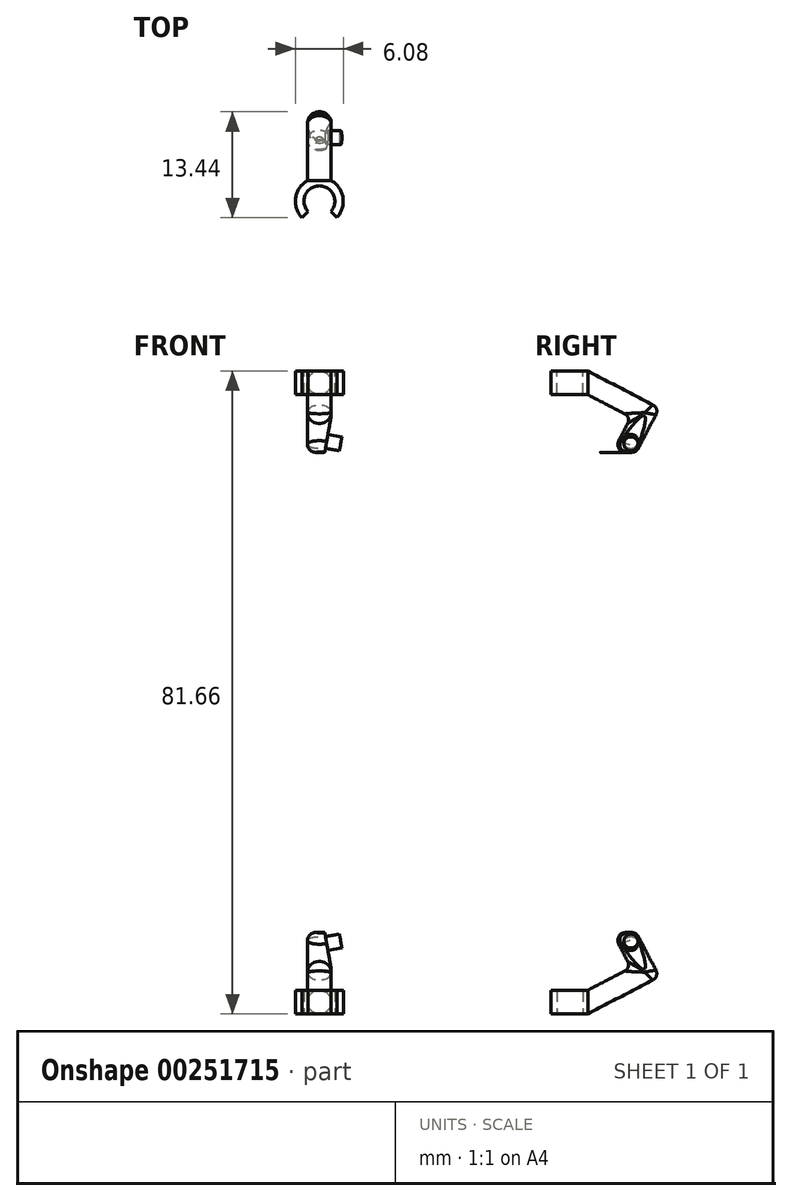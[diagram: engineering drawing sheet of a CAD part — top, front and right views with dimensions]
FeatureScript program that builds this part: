
annotation { "Feature Type Name" : "Feature", "Feature Type Description" : "" }
export const myFeature = defineFeature(function(context is Context, id is Id, definition is map)
    precondition{}
    {
        {
            var Q0;
            Q0=qCreatedBy(makeId("Top.planeOp"),FACE);
            var sketch = newSketch(context, id + "F0", { "sketchPlane" : qUnion([Q0])});
            skCircle(sketch, "E0", {"center": v(0, 0) * mm, "radius": 5 * mm});
            skSolve(sketch);
        }
        {
            var Q0;
            Q0=qCreatedBy(makeId("Right.planeOp"),FACE);
            var sketch = newSketch(context, id + "F1", { "sketchPlane" : qUnion([Q0])});
            skLineSegment(sketch, "E1", {"start": v(0, 0) * mm, "end": v(8.74, -16.81) * mm});
            skLineSegment(sketch, "E2", {"start": v(8.74, -16.81) * mm, "end": v(-15.53, -29.43) * mm});
            skSolve(sketch);
        }
        {
            var Q0;
            Q0=makeQuery(id+"F0.imprint","IMPRINT",FACE,{"disambiguationData":[TD([[makeQuery(id+"F0.imprint","IMPRINT",EDGE,{"derivedFrom":sQuery(id+"F0.wireOp",EDGE,"E0")}),1.0]])]});
            var Q1;
            Q1=sQuery(id+"F1.wireOp",EDGE,"E1");
            var Q2;
            Q2=sQuery(id+"F1.wireOp",EDGE,"E2");
            sweep(context, id + "F2", {"profiles" : qUnion([Q0]), "path" : qUnion([Q1, Q2])});
        }
        {
            var Q0;
            Q0=makeQuery(id+"F2.opSweep","MID_CAP_EDGE",EDGE,{"disambiguationData":[OSD([sQuery(id+"F0.wireOp",EDGE,"E0"),sQuery(id+"F1.wireOp",VERTEX,"E2.start")])],"capPos":1.0});
            fillet(context, id + "F3", {"entities" : qUnion([Q0]), "radius" : 3 * mm, "tangentPropagation" : true, "allowEdgeOverflow" : false});
        }
        {
            var Q0;
            Q0=makeQuery(id+"F2.opSweep","CAP_EDGE",EDGE,{"disambiguationData":[OSD([sQuery(id+"F0.wireOp",EDGE,"E0"),sQuery(id+"F1.wireOp",VERTEX,"E1.start")])],"isStart":true});
            fillet(context, id + "F4", {"entities" : qUnion([Q0]), "radius" : 3.38 * mm, "tangentPropagation" : true, "allowEdgeOverflow" : false});
        }
        {
            var Q0;
            Q0=qCreatedBy(makeId("Front.planeOp"),FACE);
            var sketch = newSketch(context, id + "F5", { "sketchPlane" : qUnion([Q0])});
            skLineSegment(sketch, "E3", {"start": v(2.03, 1.57) * mm, "end": v(31.42, 1.57) * mm});
            skLineSegment(sketch, "E4", {"start": v(2.03, 1.57) * mm, "end": v(5.73, -19.69) * mm});
            skLineSegment(sketch, "E5", {"start": v(5.73, -19.69) * mm, "end": v(31.42, 1.57) * mm});
            skSolve(sketch);
        }
        {
            var Q0;
            Q0 = qSketchRegion(id + "F5", true);
            extrude(context, id + "F6", {"entities" : qUnion([Q0]), "operationType" : NewBodyOperationType.REMOVE, "oppositeDirection" : true, "depth" : 33 * mm, "hasSecondDirection" : true, "secondDirectionOppositeDirection" : false, "secondDirectionDepth" : 37.2 * mm});
        }
        {
            var Q0;
            Q0=makeQuery(id+"F2.opSweep","CAP_FACE",FACE,{"disambiguationData":[OSD([sQuery(id+"F0.wireOp",EDGE,"E0"),sQuery(id+"F1.wireOp",VERTEX,"E2.end")])],"isStart":false});
            var sketch = newSketch(context, id + "F7", { "sketchPlane" : qUnion([Q0])});
            skCircle(sketch, "E6.0.0", {"center": v(0, -29.43) * mm, "radius": 5 * mm, "construction": true});
            skLineSegment(sketch, "E7", {"start": v(-11.73, -29.43) * mm, "end": v(10.87, -29.43) * mm, "construction": true});
            skSolve(sketch);
        }
        {
            var Q0;
            Q0=sQuery(id+"F7.wireOp",EDGE,"E7");
            cPlane(context, id + "F8", {"entities" : qUnion([Q0]), "cplaneType" : CPlaneType.LINE_ANGLE, "offset" : 25 * mm, "angle" : 90 * degree, "width" : 150 * mm, "height" : 150 * mm});
        }
        {
            var Q0;
            Q0=qCreatedBy(id+"F8.planeOp",FACE);
            var sketch = newSketch(context, id + "F9", { "sketchPlane" : qUnion([Q0])});
            skLineSegment(sketch, "E8.0", {"start": v(-11.73, -15.53) * mm, "end": v(10.87, -15.53) * mm});
            skArc(sketch, "E9", {"start": v(7.4, -31.14) * mm, "mid": v(10.02, -22.8) * mm, "end": v(5.17, -15.53) * mm});
            skArc(sketch, "E10", {"start": v(4.89, -28.57) * mm, "mid": v(0, -17.69) * mm, "end": v(-4.89, -28.57) * mm});
            skLineSegment(sketch, "E11", {"start": v(-7.4, -31.14) * mm, "end": v(-4.89, -28.57) * mm});
            skLineSegment(sketch, "E12", {"start": v(4.89, -28.57) * mm, "end": v(7.4, -31.14) * mm});
            skPoint(sketch, "E13", {"position": v(0, -30.77) * mm});
            skArc(sketch, "E14.trimOffspring", {"start": v(-5.17, -15.53) * mm, "mid": v(-10.02, -22.8) * mm, "end": v(-7.4, -31.14) * mm});
            skSolve(sketch);
        }
        {
            var Q0;
            {var subQ0=sQuery(id+"F9.wireOp",EDGE,"E9");Q0=makeQuery(id+"F9.imprint","IMPRINT",FACE,{"disambiguationData":[TD([[makeQuery(id+"F9.imprint","IMPRINT",EDGE,{"derivedFrom":subQ0}),1.0]])]});}
            extrude(context, id + "F10", {"entities" : qUnion([Q0]), "operationType" : NewBodyOperationType.ADD, "endBound" : BoundingType.SYMMETRIC, "depth" : 10 * mm});
        }
        {
            var Q0;
            Q0=qCreatedBy(makeId("Right.planeOp"),FACE);
            var sketch = newSketch(context, id + "F11", { "sketchPlane" : qUnion([Q0])});
            skLineSegment(sketch, "E15", {"start": v(-39.9, 13.4) * mm, "end": v(66.3, 13.4) * mm});
            skSolve(sketch);
        }
        {
            var Q0;
            Q0=sQuery(id+"F11.wireOp",EDGE,"E15");
            cPlane(context, id + "F12", {"entities" : qUnion([Q0]), "cplaneType" : CPlaneType.LINE_ANGLE, "offset" : 25 * mm, "angle" : 0 * degree, "width" : 150 * mm, "height" : 150 * mm});
        }
        {
            var Q0;
            Q0=makeQuery(id+"F2.opSweep","SWEPT_BODY",BODY,{"disambiguationData":[OSD([sQuery(id+"F0.wireOp",EDGE,"E0"),sQuery(id+"F1.wireOp",EDGE,"E2")])]});
            var Q1;
            {var subQ0=sQuery(id+"F9.wireOp",EDGE,"E8.0");Q1=makeQuery(id+"F10.boolean.opBoolean","TWEAK_VERTEX",VERTEX,{"derivedFrom":[makeQuery(id+"F2.opSweep","SWEPT_FACE",FACE,{"disambiguationData":[OSD([sQuery(id+"F0.wireOp",EDGE,"E0"),sQuery(id+"F1.wireOp",EDGE,"E2")])]}),makeQuery(id+"F10.opExtrude","SWEPT_FACE",FACE,{"disambiguationData":[OSD([subQ0])]}),makeQuery(id+"F10.opExtrude","CAP_FACE",FACE,{"disambiguationData":[OSD([subQ0,sQuery(id+"F9.wireOp",EDGE,"E9"),sQuery(id+"F9.wireOp",EDGE,"E10"),sQuery(id+"F9.wireOp",EDGE,"E11"),sQuery(id+"F9.wireOp",EDGE,"E12"),sQuery(id+"F9.wireOp",EDGE,"E14.trimOffspring")])],"isStart":false})]});}
            transform(context, id + "F13", {"entities" : qUnion([Q0]), "transformType" : TransformType.SCALE_UNIFORMLY, "scale" : 0.3, "scalePoint" : qUnion([Q1]), "makeCopy" : false});
        }
        {
            var Q0;
            Q0=makeQuery(id+"F6.boolean.opBoolean","COPY",FACE,{"derivedFrom":makeQuery(id+"F6.opExtrude","SWEPT_FACE",FACE,{"disambiguationData":[OSD([sQuery(id+"F5.wireOp",EDGE,"E4")])]})});
            var sketch = newSketch(context, id + "F14", { "sketchPlane" : qUnion([Q0])});
            skFitSpline(sketch, "E16.0.0", {"points": [v(-11.88, -17.49) * mm, v(-11.77, -17.67) * mm, v(-11.55, -18.02) * mm, v(-11.21, -18.54) * mm, v(-10.87, -19.06) * mm, v(-10.51, -19.57) * mm, v(-10.2, -20) * mm, v(-9.95, -20.32) * mm, v(-9.76, -20.56) * mm, v(-9.56, -20.8) * mm, v(-9.35, -21.04) * mm, v(-9.13, -21.26) * mm, v(-8.94, -21.43) * mm, v(-8.78, -21.56) * mm, v(-8.64, -21.64) * mm, v(-8.51, -21.68) * mm, v(-8.4, -21.68) * mm, v(-8.33, -21.65) * mm, v(-8.28, -21.6) * mm, v(-8.23, -21.5) * mm, v(-8.21, -21.36) * mm, v(-8.2, -21.2) * mm, v(-8.21, -21.05) * mm, v(-8.23, -20.9) * mm, v(-8.26, -20.7) * mm, v(-8.32, -20.44) * mm, v(-8.4, -20.13) * mm, v(-8.5, -19.74) * mm, v(-8.66, -19.24) * mm, v(-8.87, -18.65) * mm, v(-9.09, -18.07) * mm, v(-9.24, -17.68) * mm, v(-9.32, -17.49) * mm]});
            skFitSpline(sketch, "E16.0.1", {"points": [v(-9.28, -17.58) * mm, v(-9.3, -17.51) * mm, v(-9.38, -17.39) * mm, v(-9.58, -17.18) * mm, v(-9.84, -17.05) * mm, v(-10.12, -17) * mm, v(-10.4, -16.98) * mm, v(-10.76, -17.01) * mm, v(-11.16, -17.2) * mm, v(-11.43, -17.55) * mm, v(-11.5, -17.98) * mm, v(-11.4, -18.26) * mm, v(-11.32, -18.38) * mm]});
            skCircle(sketch, "E17", {"center": v(-10.06, -18.38) * mm, "radius": 0.9 * mm});
            skSolve(sketch);
        }
        {
            var Q0;
            Q0=makeQuery(id+"F14.imprint","IMPRINT",FACE,{"disambiguationData":[TD([[makeQuery(id+"F14.imprint","IMPRINT",EDGE,{"derivedFrom":sQuery(id+"F14.wireOp",EDGE,"E17")}),1.0]])]});
            extrude(context, id + "F15", {"entities" : qUnion([Q0]), "operationType" : NewBodyOperationType.ADD, "depth" : 1.8 * mm});
        }
        {
            var Q0;
            Q0=makeQuery(id+"F2.opSweep","SWEPT_BODY",BODY,{"disambiguationData":[OSD([sQuery(id+"F0.wireOp",EDGE,"E0"),sQuery(id+"F1.wireOp",EDGE,"E2")])]});
            var Q1;
            Q1=qCreatedBy(id+"F12.planeOp",FACE);
            mirror(context, id + "F16", {"entities" : qUnion([Q0]), "mirrorPlane" : qUnion([Q1])});
        }
    });
